# Revit family: M_Valve_Balancing and Control_MEPcontent_Oventrop_Hydrocontrol VTR 10602
name_source: partatom
category: Pipe Accessories
revit_build: Autodesk Revit 2015 (Build: 20140223_1515(x64)
units: mm (PartAtom-declared; Revit-internal decimal feet)

## types (7) — shared parameters
Angle = 50.00°
Article Description = Bronze double regulating and commissioning valves
Article Type = Hydrocontrol VTR 10602
Black = Color RGB 35-35-35
Bronze = Color RGB 156-122-90
Content Supplier URL = www.mepcontent.eu
Custom = No
Description = Bronze double regulating and commissioning valves
EMCS Version = 2.0
ETIM Article Class = EC011463
Family Version = 10.14
Hb4 = 18 mm
Hb5 = 3 mm  [stored 0.00984252 ft]
Hlp1 = 22 mm
IFCExportAs = IfcValveType
IFCExportType = PRESSUREREDUCING
Lgt2 = 11 mm  [stored 0.0360892 ft]
MEPcontent Class = VALVE_BALANCING
Manufacturer = Oventrop
Manufacturer URL = http://www.oventrop.de
Model = Hydrocontrol VTR 10602
Pressure Drop = 0.0 Pa
Product Line = Oventrop
Revit Version = 2015
URL = www.stabiplan.com
r1 = 2 mm  [stored 0.00656168 ft]
r2 = 3 mm  [stored 0.00984252 ft]

## per-type parameters (varying)
| type | GTIN | Hb1 | Hb3 | Height | L2 | Lenght | Lgt1 | Manufacturer Art. No. | NominalDiameter | NutDimension | OuterDiameter | Rad1 | Rad2 | Rad3 | Rad4 | Rad5 | SW2 | Threaded_Lenght | e2 | e3 |
| DN 40 | 4026755125115 | 154 mm | 5 mm  [stored 0.0164042 ft] | 138 mm | 9.466 mm | 120 mm | 21.1 mm | 1060212 | 38.100 mm | 55 mm | 48.3 mm | 22.3 mm | 20.3 mm | 22.8 mm | 25.3 mm | 27.3 mm | 63.509 mm | 19.1 mm | 4.5 mm  [stored 0.0147638 ft] | 2.344 mm |
| DN 50 | 4026755125122 | 167 mm | 15 mm  [stored 0.0492126 ft] | 148 mm | 13.15 mm | 150 mm | 27.7 mm | 1060216 | 50.800 mm | 70 mm | 60.3 mm | 30.2 mm | 28.2 mm | 30.7 mm | 33.2 mm | 35.2 mm | 80.829 mm | 25.7 mm | 4.5 mm  [stored 0.0147638 ft] | 2.656 mm |
| DN 32 | 4026755125108 | 151 mm | 1 mm  [stored 0.00328084 ft] | 136 mm | 7.927 mm | 110 mm | 21.1 mm | 1060210 | 31.750 mm | 50 mm | 42.4 mm | 19 mm | 17 mm  [stored 0.0557743 ft] | 19.5 mm | 22 mm | 24 mm | 57.735 mm | 19.1 mm | 4.5 mm  [stored 0.0147638 ft] | 2 mm  [stored 0.00656168 ft] |
| DN 25 | 4026755125092 | 129 mm | 13 mm | 119 mm | 6.482 mm | 97.5 mm | 18.8 mm | 1060208 | 25.400 mm | 41 mm | 33.7 mm | 15.9 mm  [stored 0.0521654 ft] | 13.9 mm  [stored 0.0456037 ft] | 16.4 mm | 18.9 mm | 20.9 mm | 47.343 mm | 16.8 mm  [stored 0.0551181 ft] | 3.5 mm  [stored 0.0114829 ft] | 1.688 mm |
| DN 20 | 4026755125085 | 125 mm | 11 mm  [stored 0.0360892 ft] | 116 mm | 4.989 mm | 84 mm | 16.5 mm  [stored 0.0541339 ft] | 1060206 | 19.050 mm | 32 mm | 26.9 mm | 12.7 mm  [stored 0.0416667 ft] | 10.7 mm  [stored 0.035105 ft] | 13.2 mm  [stored 0.0433071 ft] | 15.7 mm | 17.7 mm | 36.95 mm | 14.5 mm  [stored 0.0475722 ft] | 3.5 mm  [stored 0.0114829 ft] | 1.5 mm  [stored 0.00492126 ft] |
| DN 15 | 4026755125078 | 122 mm | 15 mm  [stored 0.0492126 ft] | 114 mm | 3.497 mm | 80 mm | 15.2 mm | 1060204 | 12.700 mm | 27 mm | 21.3 mm | 9.5 mm  [stored 0.031168 ft] | 7.5 mm  [stored 0.0246063 ft] | 10 mm  [stored 0.0328084 ft] | 12.5 mm  [stored 0.0410105 ft] | 14.5 mm  [stored 0.0475722 ft] | 31.177 mm | 13.2 mm  [stored 0.0433071 ft] | 2.5 mm  [stored 0.0082021 ft] | 1.25 mm  [stored 0.00410105 ft] |
| DN 10 | 4026755125061 | 122 mm | 15 mm  [stored 0.0492126 ft] | 114 mm | 3.497 mm | 73 mm | 12.1 mm | 1060203 | 9.525 mm | 27 mm | 17.2 mm | 9.5 mm  [stored 0.031168 ft] | 7.5 mm  [stored 0.0246063 ft] | 10 mm  [stored 0.0328084 ft] | 12.5 mm  [stored 0.0410105 ft] | 14.5 mm  [stored 0.0475722 ft] | 31.177 mm | 10.1 mm | 2.5 mm  [stored 0.0082021 ft] | 1.125 mm  [stored 0.00369095 ft] |

note: [stored X ft] marks values corroborated as IEEE doubles in the binary element streams (Revit-internal decimal feet)

## geometry (parser evidence)
native form markers: Sweep x3
no freeform markers — native parametric forms only
